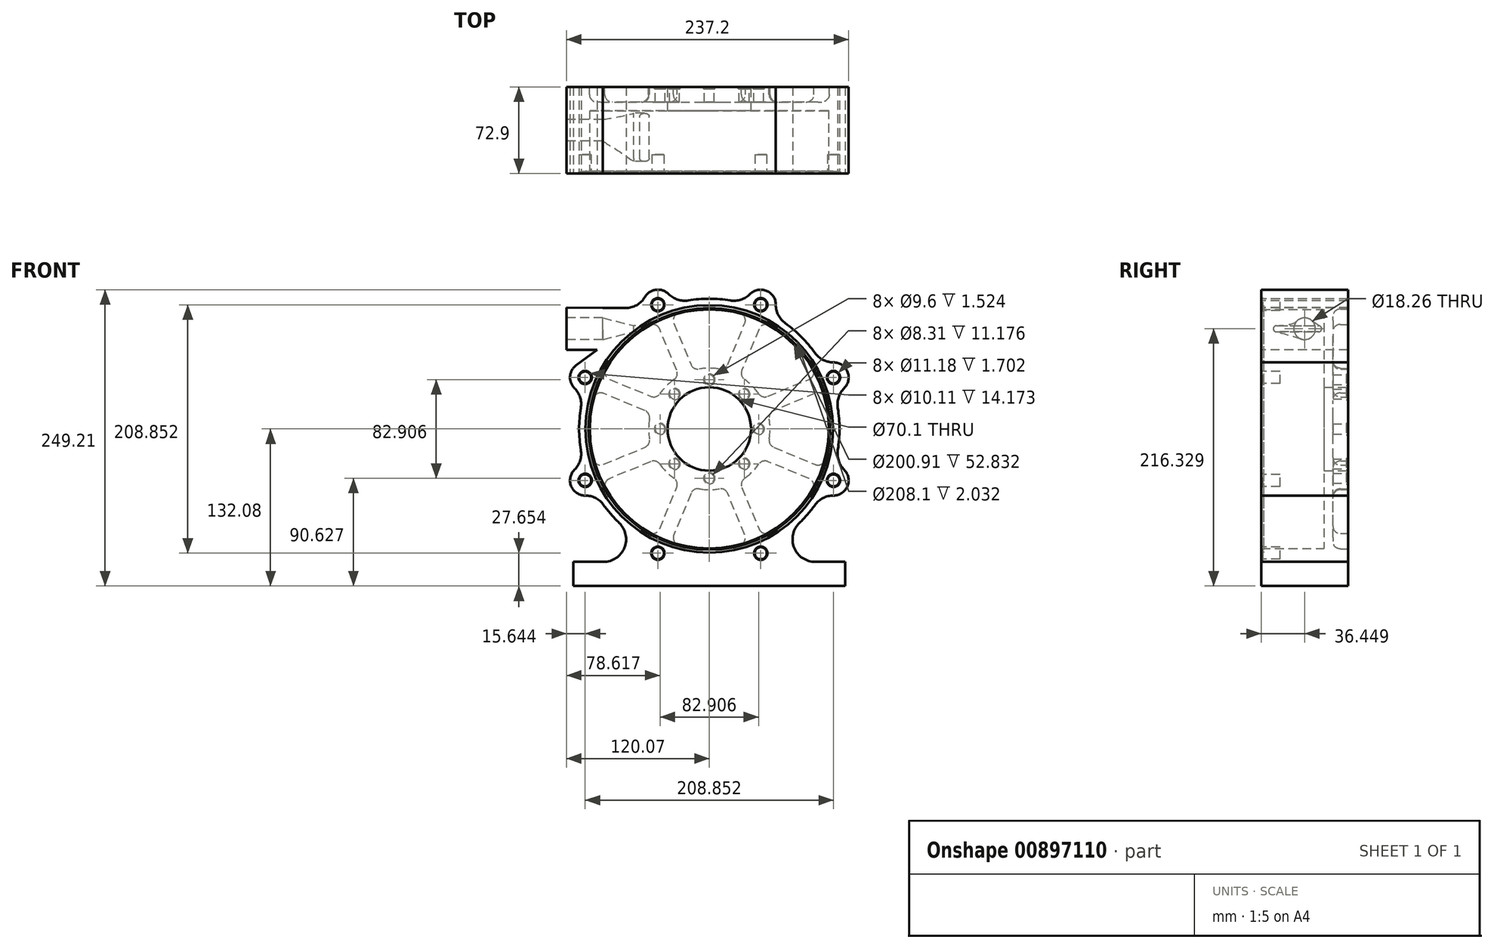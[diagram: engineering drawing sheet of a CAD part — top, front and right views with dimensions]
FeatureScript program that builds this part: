
annotation { "Feature Type Name" : "Feature", "Feature Type Description" : "" }
export const myFeature = defineFeature(function(context is Context, id is Id, definition is map)
    precondition{}
    {
        {
            var Q0;
            Q0=qCreatedBy(makeId("Front.planeOp"),FACE);
            var sketch = newSketch(context, id + "F0", { "sketchPlane" : qUnion([Q0])});
            skCircle(sketch, "E0", {"center": v(0, 0) * mm, "radius": 50.17 * mm, "construction": true});
            skArc(sketch, "E1", {"start": v(54.02, -8.84) * mm, "mid": v(54.74, 0) * mm, "end": v(54.02, 8.84) * mm});
            skCircle(sketch, "E2.cCircle", {"center": v(0, 0) * mm, "radius": 56.52 * mm, "construction": true});
            skLineSegment(sketch, "E2.0", {"start": v(52.21, -21.63) * mm, "end": v(21.63, -52.21) * mm, "construction": true});
            skLineSegment(sketch, "E2.1", {"start": v(21.63, -52.21) * mm, "end": v(-21.63, -52.21) * mm, "construction": true});
            skLineSegment(sketch, "E2.2", {"start": v(-21.63, -52.21) * mm, "end": v(-52.21, -21.63) * mm, "construction": true});
            skLineSegment(sketch, "E2.3", {"start": v(-52.21, -21.63) * mm, "end": v(-52.21, 21.63) * mm, "construction": true});
            skLineSegment(sketch, "E2.4", {"start": v(-52.21, 21.63) * mm, "end": v(-21.63, 52.21) * mm, "construction": true});
            skLineSegment(sketch, "E2.5", {"start": v(-21.63, 52.21) * mm, "end": v(21.63, 52.21) * mm, "construction": true});
            skLineSegment(sketch, "E2.6", {"start": v(21.63, 52.21) * mm, "end": v(52.21, 21.63) * mm, "construction": true});
            skLineSegment(sketch, "E2.7", {"start": v(52.21, 21.63) * mm, "end": v(52.21, -21.63) * mm, "construction": true});
            skArc(sketch, "E3", {"start": v(27.98, 52.2) * mm, "mid": v(24.06, 58.08) * mm, "end": v(17.13, 56.7) * mm});
            skArc(sketch, "E4", {"start": v(56.7, 17.13) * mm, "mid": v(58.08, 24.06) * mm, "end": v(52.2, 27.98) * mm});
            skArc(sketch, "E5", {"start": v(52.2, -27.98) * mm, "mid": v(58.08, -24.06) * mm, "end": v(56.7, -17.13) * mm});
            skArc(sketch, "E6", {"start": v(-56.7, -17.13) * mm, "mid": v(-58.08, -24.06) * mm, "end": v(-52.2, -27.98) * mm});
            skArc(sketch, "E7", {"start": v(-56, 26.73) * mm, "mid": v(-58.55, 22.09) * mm, "end": v(-56.7, 17.13) * mm});
            skArc(sketch, "E8.trimOffspring", {"start": v(44.45, 31.94) * mm, "mid": v(38.7, 38.7) * mm, "end": v(31.94, 44.45) * mm});
            skArc(sketch, "E9.trimOffspring", {"start": v(8.84, 54.02) * mm, "mid": v(0, 54.74) * mm, "end": v(-8.84, 54.02) * mm});
            skArc(sketch, "E10.trimOffspring", {"start": v(-54.02, 8.84) * mm, "mid": v(-54.74, 0) * mm, "end": v(-54.02, -8.84) * mm});
            skArc(sketch, "E11.trimOffspring", {"start": v(-44.45, -31.94) * mm, "mid": v(-41.35, -35.86) * mm, "end": v(-37.9, -39.48) * mm});
            skArc(sketch, "E12.trimOffspring", {"start": v(37.9, -39.48) * mm, "mid": v(41.35, -35.86) * mm, "end": v(44.45, -31.94) * mm});
            skLineSegment(sketch, "E13", {"start": v(-57.15, -55.88) * mm, "end": v(-57.15, -66.04) * mm});
            skLineSegment(sketch, "E14", {"start": v(-57.15, -66.04) * mm, "end": v(57.15, -66.04) * mm});
            skLineSegment(sketch, "E15", {"start": v(57.15, -66.04) * mm, "end": v(57.15, -55.88) * mm});
            skLineSegment(sketch, "E16", {"start": v(57.15, -55.88) * mm, "end": v(44.5, -55.88) * mm});
            skLineSegment(sketch, "E17", {"start": v(-57.15, -55.88) * mm, "end": v(-44.5, -55.88) * mm});
            skPoint(sketch, "E18", {"position": v(0, -66.04) * mm});
            skArc(sketch, "E19", {"start": v(-44.5, -55.88) * mm, "mid": v(-35.67, -49.91) * mm, "end": v(-37.9, -39.48) * mm});
            skArc(sketch, "E20", {"start": v(37.9, -39.48) * mm, "mid": v(35.67, -49.91) * mm, "end": v(44.5, -55.88) * mm});
            skPoint(sketch, "E21.visualSharp", {"position": v(-47.97, -26.36) * mm});
            skArc(sketch, "E21.filletArc", {"start": v(-44.45, -31.94) * mm, "mid": v(-47.85, -29.02) * mm, "end": v(-52.2, -27.98) * mm});
            skPoint(sketch, "E22.visualSharp", {"position": v(-52.56, -15.29) * mm});
            skArc(sketch, "E22.filletArc", {"start": v(-56.7, -17.13) * mm, "mid": v(-54.35, -13.3) * mm, "end": v(-54.02, -8.84) * mm});
            skPoint(sketch, "E23.visualSharp", {"position": v(-52.56, 15.29) * mm});
            skArc(sketch, "E23.filletArc", {"start": v(-54.02, 8.84) * mm, "mid": v(-54.35, 13.3) * mm, "end": v(-56.7, 17.13) * mm});
            skPoint(sketch, "E24.visualSharp", {"position": v(47.97, -26.36) * mm});
            skArc(sketch, "E24.filletArc", {"start": v(52.2, -27.98) * mm, "mid": v(47.85, -29.02) * mm, "end": v(44.45, -31.94) * mm});
            skPoint(sketch, "E25.visualSharp", {"position": v(52.56, -15.29) * mm});
            skArc(sketch, "E25.filletArc", {"start": v(54.02, -8.84) * mm, "mid": v(54.35, -13.3) * mm, "end": v(56.7, -17.13) * mm});
            skPoint(sketch, "E26.visualSharp", {"position": v(52.56, 15.29) * mm});
            skArc(sketch, "E26.filletArc", {"start": v(56.7, 17.13) * mm, "mid": v(54.35, 13.3) * mm, "end": v(54.02, 8.84) * mm});
            skPoint(sketch, "E27.visualSharp", {"position": v(47.97, 26.36) * mm});
            skArc(sketch, "E27.filletArc", {"start": v(44.45, 31.94) * mm, "mid": v(47.85, 29.02) * mm, "end": v(52.2, 27.98) * mm});
            skPoint(sketch, "E28.visualSharp", {"position": v(26.36, 47.97) * mm});
            skArc(sketch, "E28.filletArc", {"start": v(27.98, 52.2) * mm, "mid": v(29.02, 47.85) * mm, "end": v(31.94, 44.45) * mm});
            skPoint(sketch, "E29.visualSharp", {"position": v(15.29, 52.56) * mm});
            skArc(sketch, "E29.filletArc", {"start": v(8.84, 54.02) * mm, "mid": v(13.3, 54.35) * mm, "end": v(17.13, 56.7) * mm});
            skPoint(sketch, "E30.visualSharp", {"position": v(-15.29, 52.56) * mm});
            skLineSegment(sketch, "E31", {"start": v(-35.27, 50.8) * mm, "end": v(-44.8, 50.8) * mm});
            skArc(sketch, "E32", {"start": v(-17.13, 56.7) * mm, "mid": v(-22.41, 58.51) * mm, "end": v(-27.09, 55.46) * mm});
            skArc(sketch, "E33.filletArc", {"start": v(-17.13, 56.7) * mm, "mid": v(-13.3, 54.35) * mm, "end": v(-8.84, 54.02) * mm});
            skPoint(sketch, "E34.visualSharp", {"position": v(-27.82, 50.8) * mm});
            skArc(sketch, "E34.filletArc", {"start": v(-35.27, 50.8) * mm, "mid": v(-30.56, 52.05) * mm, "end": v(-27.09, 55.46) * mm});
            skLineSegment(sketch, "E35", {"start": v(-47.22, 33.23) * mm, "end": v(-56, 26.73) * mm});
            skLineSegment(sketch, "E36", {"start": v(-44.8, 50.8) * mm, "end": v(-60.04, 51.01) * mm});
            skLineSegment(sketch, "E37", {"start": v(-60.04, 51.01) * mm, "end": v(-60.04, 33.23) * mm});
            skLineSegment(sketch, "E38", {"start": v(-60.04, 33.23) * mm, "end": v(-47.22, 33.23) * mm});
            skSolve(sketch);
        }
        {
            var Q0;
            Q0=qSketchRegion(id+"F0",true);
            extrude(context, id + "F1", {"entities" : qUnion([Q0]), "oppositeDirection" : true, "depth" : 36.45 * mm});
        }
        {
            var Q0;
            Q0=qCreatedBy(makeId("Right.planeOp"),FACE);
            var sketch = newSketch(context, id + "F2", { "sketchPlane" : qUnion([Q0])});
            skLineSegment(sketch, "E39", {"start": v(0, 0) * mm, "end": v(0, 50.23) * mm});
            skLineSegment(sketch, "E40", {"start": v(26.42, 50.23) * mm, "end": v(0, 50.23) * mm});
            skLineSegment(sketch, "E41", {"start": v(26.42, 50.23) * mm, "end": v(26.42, 17.53) * mm});
            skLineSegment(sketch, "E42", {"start": v(36.45, 17.53) * mm, "end": v(26.42, 17.53) * mm});
            skLineSegment(sketch, "E43", {"start": v(36.45, 17.53) * mm, "end": v(36.45, 0) * mm});
            skLineSegment(sketch, "E44", {"start": v(0, 0) * mm, "end": v(36.45, 0) * mm});
            skLineSegment(sketch, "E45.bottom", {"start": v(1.02, 50.8) * mm, "end": v(0, 50.8) * mm});
            skLineSegment(sketch, "E45.top", {"start": v(1.02, 52.03) * mm, "end": v(0, 52.03) * mm});
            skLineSegment(sketch, "E45.left", {"start": v(0, 50.8) * mm, "end": v(0, 52.03) * mm});
            skLineSegment(sketch, "E45.right", {"start": v(1.02, 50.8) * mm, "end": v(1.02, 52.03) * mm});
            skSolve(sketch);
        }
        {
            var Q0;
            Q0=qSketchRegion(id+"F2",true);
            var Q1;
            Q1=sQuery(id+"F2.wireOp",EDGE,"E44");
            revolve(context, id + "F3", {"operationType" : NewBodyOperationType.REMOVE, "entities" : qUnion([Q0]), "axis" : qUnion([Q1]), "revolveType" : RevolveType.FULL, "oppositeDirection" : true});
        }
        {
            var Q0;
            Q0=makeQuery(id+"F1.opExtrude","CAP_FACE",FACE,{"disambiguationData":[OSD([sQuery(id+"F0.wireOp",EDGE,"E1"),sQuery(id+"F0.wireOp",EDGE,"E3"),sQuery(id+"F0.wireOp",EDGE,"E4"),sQuery(id+"F0.wireOp",EDGE,"E5"),sQuery(id+"F0.wireOp",EDGE,"E6"),sQuery(id+"F0.wireOp",EDGE,"E7"),sQuery(id+"F0.wireOp",EDGE,"E8.trimOffspring"),sQuery(id+"F0.wireOp",EDGE,"E9.trimOffspring"),sQuery(id+"F0.wireOp",EDGE,"E10.trimOffspring"),sQuery(id+"F0.wireOp",EDGE,"E11.trimOffspring"),sQuery(id+"F0.wireOp",EDGE,"E12.trimOffspring"),sQuery(id+"F0.wireOp",EDGE,"E13"),sQuery(id+"F0.wireOp",EDGE,"E14"),sQuery(id+"F0.wireOp",EDGE,"E15"),sQuery(id+"F0.wireOp",EDGE,"E16"),sQuery(id+"F0.wireOp",EDGE,"E17"),sQuery(id+"F0.wireOp",EDGE,"E19"),sQuery(id+"F0.wireOp",EDGE,"E20"),sQuery(id+"F0.wireOp",EDGE,"E21.filletArc"),sQuery(id+"F0.wireOp",EDGE,"E22.filletArc"),sQuery(id+"F0.wireOp",EDGE,"E23.filletArc"),sQuery(id+"F0.wireOp",EDGE,"E24.filletArc"),sQuery(id+"F0.wireOp",EDGE,"E25.filletArc"),sQuery(id+"F0.wireOp",EDGE,"E26.filletArc"),sQuery(id+"F0.wireOp",EDGE,"E27.filletArc"),sQuery(id+"F0.wireOp",EDGE,"E28.filletArc"),sQuery(id+"F0.wireOp",EDGE,"E29.filletArc"),sQuery(id+"F0.wireOp",EDGE,"E31"),sQuery(id+"F0.wireOp",EDGE,"kHr8fFUD-4EFk-nJZE-7JVT-0WPmz8yTTr2E"),sQuery(id+"F0.wireOp",EDGE,"E32"),sQuery(id+"F0.wireOp",EDGE,"E33.filletArc"),sQuery(id+"F0.wireOp",EDGE,"E34.filletArc"),sQuery(id+"F0.wireOp",EDGE,"fBgQRkSS-CIUt-JJdx-RIVp-XrYWp9c1mPRc"),sQuery(id+"F0.wireOp",EDGE,"E35")])],"isStart":false});
            var sketch = newSketch(context, id + "F4", { "sketchPlane" : qUnion([Q0])});
            skPoint(sketch, "E46.center", {"position": v(0, 0) * mm});
            skArc(sketch, "E47", {"start": v(4.25, 25.17) * mm, "mid": v(0, 25.53) * mm, "end": v(-4.25, 25.17) * mm});
            skLineSegment(sketch, "E48", {"start": v(0, 0) * mm, "end": v(24.06, 58.08) * mm, "construction": true});
            skLineSegment(sketch, "E49", {"start": v(0, 0) * mm, "end": v(0, 17.53) * mm, "construction": true});
            skArc(sketch, "E50", {"start": v(12.8, 48.77) * mm, "mid": v(0, 50.42) * mm, "end": v(-12.8, 48.77) * mm});
            skLineSegment(sketch, "E51", {"start": v(14.92, 44.48) * mm, "end": v(7.71, 27.09) * mm});
            skLineSegment(sketch, "E52", {"start": v(-7.71, 27.09) * mm, "end": v(-14.92, 44.48) * mm});
            skPoint(sketch, "E53.visualSharp", {"position": v(-16.26, 47.72) * mm});
            skArc(sketch, "E53.filletArc", {"start": v(-12.8, 48.77) * mm, "mid": v(-14.83, 47.1) * mm, "end": v(-14.92, 44.48) * mm});
            skPoint(sketch, "E54.visualSharp", {"position": v(16.26, 47.72) * mm});
            skArc(sketch, "E54.filletArc", {"start": v(14.92, 44.48) * mm, "mid": v(14.83, 47.1) * mm, "end": v(12.8, 48.77) * mm});
            skPoint(sketch, "E55.visualSharp", {"position": v(6.7, 24.63) * mm});
            skArc(sketch, "E55.filletArc", {"start": v(4.25, 25.17) * mm, "mid": v(6.32, 25.52) * mm, "end": v(7.71, 27.09) * mm});
            skPoint(sketch, "E56.visualSharp", {"position": v(-6.7, 24.63) * mm});
            skArc(sketch, "E56.filletArc", {"start": v(-7.71, 27.09) * mm, "mid": v(-6.32, 25.52) * mm, "end": v(-4.25, 25.17) * mm});
            skArc(sketch, "E57.1.0", {"start": v(-43.53, 25.44) * mm, "mid": v(-43.8, 22.82) * mm, "end": v(-42, 20.9) * mm});
            skLineSegment(sketch, "E57.1.1", {"start": v(-24.6, 13.7) * mm, "end": v(-42, 20.9) * mm});
            skArc(sketch, "E57.1.2", {"start": v(-14.8, 20.8) * mm, "mid": v(-18.05, 18.05) * mm, "end": v(-20.8, 14.8) * mm});
            skArc(sketch, "E57.1.3", {"start": v(-24.6, 13.7) * mm, "mid": v(-22.51, 13.58) * mm, "end": v(-20.8, 14.8) * mm});
            skArc(sketch, "E57.1.4", {"start": v(-14.8, 20.8) * mm, "mid": v(-13.58, 22.51) * mm, "end": v(-13.7, 24.6) * mm});
            skLineSegment(sketch, "E57.1.5", {"start": v(-20.9, 42) * mm, "end": v(-13.7, 24.6) * mm});
            skArc(sketch, "E57.1.6", {"start": v(-20.9, 42) * mm, "mid": v(-22.82, 43.8) * mm, "end": v(-25.44, 43.53) * mm});
            skArc(sketch, "E57.1.7", {"start": v(-25.44, 43.53) * mm, "mid": v(-35.65, 35.65) * mm, "end": v(-43.53, 25.44) * mm});
            skArc(sketch, "E57.2.0", {"start": v(-48.77, -12.8) * mm, "mid": v(-47.1, -14.83) * mm, "end": v(-44.48, -14.92) * mm});
            skLineSegment(sketch, "E57.2.1", {"start": v(-27.09, -7.71) * mm, "end": v(-44.48, -14.92) * mm});
            skArc(sketch, "E57.2.2", {"start": v(-25.17, 4.25) * mm, "mid": v(-25.53, 0) * mm, "end": v(-25.17, -4.25) * mm});
            skArc(sketch, "E57.2.3", {"start": v(-27.09, -7.71) * mm, "mid": v(-25.52, -6.32) * mm, "end": v(-25.17, -4.25) * mm});
            skArc(sketch, "E57.2.4", {"start": v(-25.17, 4.25) * mm, "mid": v(-25.52, 6.32) * mm, "end": v(-27.09, 7.71) * mm});
            skLineSegment(sketch, "E57.2.5", {"start": v(-44.48, 14.92) * mm, "end": v(-27.09, 7.71) * mm});
            skArc(sketch, "E57.2.6", {"start": v(-44.48, 14.92) * mm, "mid": v(-47.1, 14.83) * mm, "end": v(-48.77, 12.8) * mm});
            skArc(sketch, "E57.2.7", {"start": v(-48.77, 12.8) * mm, "mid": v(-50.42, 0) * mm, "end": v(-48.77, -12.8) * mm});
            skArc(sketch, "E57.3.0", {"start": v(-25.44, -43.53) * mm, "mid": v(-22.82, -43.8) * mm, "end": v(-20.9, -42) * mm});
            skLineSegment(sketch, "E57.3.1", {"start": v(-13.7, -24.6) * mm, "end": v(-20.9, -42) * mm});
            skArc(sketch, "E57.3.2", {"start": v(-20.8, -14.8) * mm, "mid": v(-18.05, -18.05) * mm, "end": v(-14.8, -20.8) * mm});
            skArc(sketch, "E57.3.3", {"start": v(-13.7, -24.6) * mm, "mid": v(-13.58, -22.51) * mm, "end": v(-14.8, -20.8) * mm});
            skArc(sketch, "E57.3.4", {"start": v(-20.8, -14.8) * mm, "mid": v(-22.51, -13.58) * mm, "end": v(-24.6, -13.7) * mm});
            skLineSegment(sketch, "E57.3.5", {"start": v(-42, -20.9) * mm, "end": v(-24.6, -13.7) * mm});
            skArc(sketch, "E57.3.6", {"start": v(-42, -20.9) * mm, "mid": v(-43.8, -22.82) * mm, "end": v(-43.53, -25.44) * mm});
            skArc(sketch, "E57.3.7", {"start": v(-43.53, -25.44) * mm, "mid": v(-35.65, -35.65) * mm, "end": v(-25.44, -43.53) * mm});
            skArc(sketch, "E57.4.0", {"start": v(12.8, -48.77) * mm, "mid": v(14.83, -47.1) * mm, "end": v(14.92, -44.48) * mm});
            skLineSegment(sketch, "E57.4.1", {"start": v(7.71, -27.09) * mm, "end": v(14.92, -44.48) * mm});
            skArc(sketch, "E57.4.2", {"start": v(-4.25, -25.17) * mm, "mid": v(0, -25.53) * mm, "end": v(4.25, -25.17) * mm});
            skArc(sketch, "E57.4.3", {"start": v(7.71, -27.09) * mm, "mid": v(6.32, -25.52) * mm, "end": v(4.25, -25.17) * mm});
            skArc(sketch, "E57.4.4", {"start": v(-4.25, -25.17) * mm, "mid": v(-6.32, -25.52) * mm, "end": v(-7.71, -27.09) * mm});
            skLineSegment(sketch, "E57.4.5", {"start": v(-14.92, -44.48) * mm, "end": v(-7.71, -27.09) * mm});
            skArc(sketch, "E57.4.6", {"start": v(-14.92, -44.48) * mm, "mid": v(-14.83, -47.1) * mm, "end": v(-12.8, -48.77) * mm});
            skArc(sketch, "E57.4.7", {"start": v(-12.8, -48.77) * mm, "mid": v(0, -50.42) * mm, "end": v(12.8, -48.77) * mm});
            skArc(sketch, "E57.5.0", {"start": v(43.53, -25.44) * mm, "mid": v(43.8, -22.82) * mm, "end": v(42, -20.9) * mm});
            skLineSegment(sketch, "E57.5.1", {"start": v(24.6, -13.7) * mm, "end": v(42, -20.9) * mm});
            skArc(sketch, "E57.5.2", {"start": v(14.8, -20.8) * mm, "mid": v(18.05, -18.05) * mm, "end": v(20.8, -14.8) * mm});
            skArc(sketch, "E57.5.3", {"start": v(24.6, -13.7) * mm, "mid": v(22.51, -13.58) * mm, "end": v(20.8, -14.8) * mm});
            skArc(sketch, "E57.5.4", {"start": v(14.8, -20.8) * mm, "mid": v(13.58, -22.51) * mm, "end": v(13.7, -24.6) * mm});
            skLineSegment(sketch, "E57.5.5", {"start": v(20.9, -42) * mm, "end": v(13.7, -24.6) * mm});
            skArc(sketch, "E57.5.6", {"start": v(20.9, -42) * mm, "mid": v(22.82, -43.8) * mm, "end": v(25.44, -43.53) * mm});
            skArc(sketch, "E57.5.7", {"start": v(25.44, -43.53) * mm, "mid": v(35.65, -35.65) * mm, "end": v(43.53, -25.44) * mm});
            skArc(sketch, "E57.6.0", {"start": v(48.77, 12.8) * mm, "mid": v(47.1, 14.83) * mm, "end": v(44.48, 14.92) * mm});
            skLineSegment(sketch, "E57.6.1", {"start": v(27.09, 7.71) * mm, "end": v(44.48, 14.92) * mm});
            skArc(sketch, "E57.6.2", {"start": v(25.17, -4.25) * mm, "mid": v(25.53, 0) * mm, "end": v(25.17, 4.25) * mm});
            skArc(sketch, "E57.6.3", {"start": v(27.09, 7.71) * mm, "mid": v(25.52, 6.32) * mm, "end": v(25.17, 4.25) * mm});
            skArc(sketch, "E57.6.4", {"start": v(25.17, -4.25) * mm, "mid": v(25.52, -6.32) * mm, "end": v(27.09, -7.71) * mm});
            skLineSegment(sketch, "E57.6.5", {"start": v(44.48, -14.92) * mm, "end": v(27.09, -7.71) * mm});
            skArc(sketch, "E57.6.6", {"start": v(44.48, -14.92) * mm, "mid": v(47.1, -14.83) * mm, "end": v(48.77, -12.8) * mm});
            skArc(sketch, "E57.6.7", {"start": v(48.77, -12.8) * mm, "mid": v(50.42, 0) * mm, "end": v(48.77, 12.8) * mm});
            skArc(sketch, "E57.7.0", {"start": v(25.44, 43.53) * mm, "mid": v(22.82, 43.8) * mm, "end": v(20.9, 42) * mm});
            skLineSegment(sketch, "E57.7.1", {"start": v(13.7, 24.6) * mm, "end": v(20.9, 42) * mm});
            skArc(sketch, "E57.7.2", {"start": v(20.8, 14.8) * mm, "mid": v(18.05, 18.05) * mm, "end": v(14.8, 20.8) * mm});
            skArc(sketch, "E57.7.3", {"start": v(13.7, 24.6) * mm, "mid": v(13.58, 22.51) * mm, "end": v(14.8, 20.8) * mm});
            skArc(sketch, "E57.7.4", {"start": v(20.8, 14.8) * mm, "mid": v(22.51, 13.58) * mm, "end": v(24.6, 13.7) * mm});
            skLineSegment(sketch, "E57.7.5", {"start": v(42, 20.9) * mm, "end": v(24.6, 13.7) * mm});
            skArc(sketch, "E57.7.6", {"start": v(42, 20.9) * mm, "mid": v(43.8, 22.82) * mm, "end": v(43.53, 25.44) * mm});
            skArc(sketch, "E57.7.7", {"start": v(43.53, 25.44) * mm, "mid": v(35.65, 35.65) * mm, "end": v(25.44, 43.53) * mm});
            skSolve(sketch);
        }
        {
            var Q0;
            Q0=qSketchRegion(id+"F4",true);
            extrude(context, id + "F5", {"entities" : qUnion([Q0]), "operationType" : NewBodyOperationType.REMOVE, "oppositeDirection" : true, "depth" : 6.35 * mm});
        }
        {
            var Q0;
            Q0=makeQuery(id+"F5.boolean.opBoolean","COPY",FACE,{"derivedFrom":makeQuery(id+"F5.opExtrude","CAP_FACE",FACE,{"disambiguationData":[OSD([sQuery(id+"F4.wireOp",EDGE,"E47"),sQuery(id+"F4.wireOp",EDGE,"E50"),sQuery(id+"F4.wireOp",EDGE,"E51"),sQuery(id+"F4.wireOp",EDGE,"E52"),sQuery(id+"F4.wireOp",EDGE,"E53.filletArc"),sQuery(id+"F4.wireOp",EDGE,"E54.filletArc"),sQuery(id+"F4.wireOp",EDGE,"E55.filletArc"),sQuery(id+"F4.wireOp",EDGE,"E56.filletArc")])],"isStart":false})});
            var Q1;
            Q1=makeQuery(id+"F5.boolean.opBoolean","COPY",FACE,{"derivedFrom":makeQuery(id+"F5.opExtrude","CAP_FACE",FACE,{"disambiguationData":[OSD([sQuery(id+"F4.wireOp",EDGE,"E57.7.0"),sQuery(id+"F4.wireOp",EDGE,"E57.7.1"),sQuery(id+"F4.wireOp",EDGE,"E57.7.2"),sQuery(id+"F4.wireOp",EDGE,"E57.7.3"),sQuery(id+"F4.wireOp",EDGE,"E57.7.4"),sQuery(id+"F4.wireOp",EDGE,"E57.7.5"),sQuery(id+"F4.wireOp",EDGE,"E57.7.6"),sQuery(id+"F4.wireOp",EDGE,"E57.7.7")])],"isStart":false})});
            var Q2;
            Q2=makeQuery(id+"F5.boolean.opBoolean","COPY",FACE,{"derivedFrom":makeQuery(id+"F5.opExtrude","CAP_FACE",FACE,{"disambiguationData":[OSD([sQuery(id+"F4.wireOp",EDGE,"E57.6.0"),sQuery(id+"F4.wireOp",EDGE,"E57.6.1"),sQuery(id+"F4.wireOp",EDGE,"E57.6.2"),sQuery(id+"F4.wireOp",EDGE,"E57.6.3"),sQuery(id+"F4.wireOp",EDGE,"E57.6.4"),sQuery(id+"F4.wireOp",EDGE,"E57.6.5"),sQuery(id+"F4.wireOp",EDGE,"E57.6.6"),sQuery(id+"F4.wireOp",EDGE,"E57.6.7")])],"isStart":false})});
            var Q3;
            Q3=makeQuery(id+"F5.boolean.opBoolean","COPY",FACE,{"derivedFrom":makeQuery(id+"F5.opExtrude","CAP_FACE",FACE,{"disambiguationData":[OSD([sQuery(id+"F4.wireOp",EDGE,"E57.5.0"),sQuery(id+"F4.wireOp",EDGE,"E57.5.1"),sQuery(id+"F4.wireOp",EDGE,"E57.5.2"),sQuery(id+"F4.wireOp",EDGE,"E57.5.3"),sQuery(id+"F4.wireOp",EDGE,"E57.5.4"),sQuery(id+"F4.wireOp",EDGE,"E57.5.5"),sQuery(id+"F4.wireOp",EDGE,"E57.5.6"),sQuery(id+"F4.wireOp",EDGE,"E57.5.7")])],"isStart":false})});
            var Q4;
            Q4=makeQuery(id+"F5.boolean.opBoolean","COPY",FACE,{"derivedFrom":makeQuery(id+"F5.opExtrude","CAP_FACE",FACE,{"disambiguationData":[OSD([sQuery(id+"F4.wireOp",EDGE,"E57.4.0"),sQuery(id+"F4.wireOp",EDGE,"E57.4.1"),sQuery(id+"F4.wireOp",EDGE,"E57.4.2"),sQuery(id+"F4.wireOp",EDGE,"E57.4.3"),sQuery(id+"F4.wireOp",EDGE,"E57.4.4"),sQuery(id+"F4.wireOp",EDGE,"E57.4.5"),sQuery(id+"F4.wireOp",EDGE,"E57.4.6"),sQuery(id+"F4.wireOp",EDGE,"E57.4.7")])],"isStart":false})});
            var Q5;
            Q5=makeQuery(id+"F5.boolean.opBoolean","COPY",FACE,{"derivedFrom":makeQuery(id+"F5.opExtrude","CAP_FACE",FACE,{"disambiguationData":[OSD([sQuery(id+"F4.wireOp",EDGE,"E57.3.0"),sQuery(id+"F4.wireOp",EDGE,"E57.3.1"),sQuery(id+"F4.wireOp",EDGE,"E57.3.2"),sQuery(id+"F4.wireOp",EDGE,"E57.3.3"),sQuery(id+"F4.wireOp",EDGE,"E57.3.4"),sQuery(id+"F4.wireOp",EDGE,"E57.3.5"),sQuery(id+"F4.wireOp",EDGE,"E57.3.6"),sQuery(id+"F4.wireOp",EDGE,"E57.3.7")])],"isStart":false})});
            var Q6;
            Q6=makeQuery(id+"F5.boolean.opBoolean","COPY",FACE,{"derivedFrom":makeQuery(id+"F5.opExtrude","CAP_FACE",FACE,{"disambiguationData":[OSD([sQuery(id+"F4.wireOp",EDGE,"E57.2.0"),sQuery(id+"F4.wireOp",EDGE,"E57.2.1"),sQuery(id+"F4.wireOp",EDGE,"E57.2.2"),sQuery(id+"F4.wireOp",EDGE,"E57.2.3"),sQuery(id+"F4.wireOp",EDGE,"E57.2.4"),sQuery(id+"F4.wireOp",EDGE,"E57.2.5"),sQuery(id+"F4.wireOp",EDGE,"E57.2.6"),sQuery(id+"F4.wireOp",EDGE,"E57.2.7")])],"isStart":false})});
            var Q7;
            Q7=makeQuery(id+"F5.boolean.opBoolean","COPY",FACE,{"derivedFrom":makeQuery(id+"F5.opExtrude","CAP_FACE",FACE,{"disambiguationData":[OSD([sQuery(id+"F4.wireOp",EDGE,"E57.1.0"),sQuery(id+"F4.wireOp",EDGE,"E57.1.1"),sQuery(id+"F4.wireOp",EDGE,"E57.1.2"),sQuery(id+"F4.wireOp",EDGE,"E57.1.3"),sQuery(id+"F4.wireOp",EDGE,"E57.1.4"),sQuery(id+"F4.wireOp",EDGE,"E57.1.5"),sQuery(id+"F4.wireOp",EDGE,"E57.1.6"),sQuery(id+"F4.wireOp",EDGE,"E57.1.7")])],"isStart":false})});
            fillet(context, id + "F6", {"entities" : qUnion([Q0, Q1, Q2, Q3, Q4, Q5, Q6, Q7]), "radius" : 3.17 * mm, "tangentPropagation" : true, "allowEdgeOverflow" : false});
        }
        {
            var Q0;
            Q0=makeQuery(id+"F1.opExtrude","SWEPT_FACE",FACE,{"disambiguationData":[OSD([sQuery(id+"F0.wireOp",EDGE,"E37")])]});
            var sketch = newSketch(context, id + "F7", { "sketchPlane" : qUnion([Q0])});
            skCircle(sketch, "E58", {"center": v(-18.22, 42.12) * mm, "radius": 4.56 * mm});
            skPoint(sketch, "E59", {"position": v(-18.22, 51.01) * mm});
            skPoint(sketch, "E60", {"position": v(0, 42.12) * mm});
            skSolve(sketch);
        }
        {
            var Q0;
            Q0=qSketchRegion(id+"F7",true);
            extrude(context, id + "F8", {"entities" : qUnion([Q0]), "operationType" : NewBodyOperationType.REMOVE, "oppositeDirection" : true, "depth" : 15.24 * mm});
        }
        {
            var Q0;
            Q0=qCreatedBy(makeId("Right.planeOp"),FACE);
            cPlane(context, id + "F9", {"entities" : qUnion([Q0]), "cplaneType" : CPlaneType.OFFSET, "offset" : 31.75 * mm, "oppositeDirection" : true, "width" : 152.4 * mm, "height" : 152.4 * mm});
        }
        {
            var Q0;
            Q0=qCreatedBy(id+"F9.planeOp",FACE);
            var sketch = newSketch(context, id + "F10", { "sketchPlane" : qUnion([Q0])});
            skLineSegment(sketch, "E61", {"start": v(6.35, 43.4) * mm, "end": v(24.13, 43.4) * mm});
            skLineSegment(sketch, "E62", {"start": v(24.13, 40.85) * mm, "end": v(6.35, 40.85) * mm});
            skArc(sketch, "E63", {"start": v(24.13, 40.85) * mm, "mid": v(25.4, 42.12) * mm, "end": v(24.13, 43.4) * mm});
            skArc(sketch, "E64", {"start": v(6.35, 43.4) * mm, "mid": v(5.08, 42.12) * mm, "end": v(6.35, 40.85) * mm});
            skPoint(sketch, "E65", {"position": v(18.22, 42.12) * mm});
            skSolve(sketch);
        }
        {
            var Q0;
            Q0=makeQuery(id+"F8.boolean.opBoolean","COPY",FACE,{"derivedFrom":makeQuery(id+"F8.opExtrude","CAP_FACE",FACE,{"disambiguationData":[OSD([sQuery(id+"F7.wireOp",EDGE,"E58")])],"isStart":false})});
            var sketch = newSketch(context, id + "F11", { "sketchPlane" : qUnion([Q0])});
            skCircle(sketch, "E66", {"center": v(-18.22, 42.12) * mm, "radius": 4.56 * mm});
            skSolve(sketch);
        }
        {
            var Q1;
            Q1=qSketchRegion(id+"F10",true);
            var Q2;
            Q2=qSketchRegion(id+"F11",true);
            loft(context, id + "F12", {"operationType" : NewBodyOperationType.REMOVE, "sheetProfilesArray" : [{ "sheetProfileEntities" : qUnion([Q1]) }, { "sheetProfileEntities" : qUnion([Q2]) }]});
        }
        {
            var Q0;
            Q0=qSketchRegion(id+"F10",true);
            extrude(context, id + "F13", {"entities" : qUnion([Q0]), "operationType" : NewBodyOperationType.REMOVE, "depth" : 25.4 * mm});
        }
        {
            var Q0;
            Q0=makeQuery(id+"F1.opExtrude","SWEPT_BODY",BODY,{"disambiguationData":[OSD([sQuery(id+"F0.wireOp",EDGE,"E1"),sQuery(id+"F0.wireOp",EDGE,"E3"),sQuery(id+"F0.wireOp",EDGE,"E4"),sQuery(id+"F0.wireOp",EDGE,"E5"),sQuery(id+"F0.wireOp",EDGE,"E6"),sQuery(id+"F0.wireOp",EDGE,"E7"),sQuery(id+"F0.wireOp",EDGE,"E8.trimOffspring"),sQuery(id+"F0.wireOp",EDGE,"E9.trimOffspring"),sQuery(id+"F0.wireOp",EDGE,"E10.trimOffspring"),sQuery(id+"F0.wireOp",EDGE,"E11.trimOffspring"),sQuery(id+"F0.wireOp",EDGE,"E12.trimOffspring"),sQuery(id+"F0.wireOp",EDGE,"E13"),sQuery(id+"F0.wireOp",EDGE,"E14"),sQuery(id+"F0.wireOp",EDGE,"E15"),sQuery(id+"F0.wireOp",EDGE,"E16"),sQuery(id+"F0.wireOp",EDGE,"E17"),sQuery(id+"F0.wireOp",EDGE,"E19"),sQuery(id+"F0.wireOp",EDGE,"E20"),sQuery(id+"F0.wireOp",EDGE,"E21.filletArc"),sQuery(id+"F0.wireOp",EDGE,"E22.filletArc"),sQuery(id+"F0.wireOp",EDGE,"E23.filletArc"),sQuery(id+"F0.wireOp",EDGE,"E24.filletArc"),sQuery(id+"F0.wireOp",EDGE,"E25.filletArc"),sQuery(id+"F0.wireOp",EDGE,"E26.filletArc"),sQuery(id+"F0.wireOp",EDGE,"E27.filletArc"),sQuery(id+"F0.wireOp",EDGE,"E28.filletArc"),sQuery(id+"F0.wireOp",EDGE,"E29.filletArc"),sQuery(id+"F0.wireOp",EDGE,"E31"),sQuery(id+"F0.wireOp",EDGE,"E32"),sQuery(id+"F0.wireOp",EDGE,"E33.filletArc"),sQuery(id+"F0.wireOp",EDGE,"E34.filletArc"),sQuery(id+"F0.wireOp",EDGE,"E35"),sQuery(id+"F0.wireOp",EDGE,"E36"),sQuery(id+"F0.wireOp",EDGE,"E37"),sQuery(id+"F0.wireOp",EDGE,"E38")])]});
            var Q1;
            Q1=qCreatedBy(makeId("Origin.pointOp"),VERTEX);
            transform(context, id + "F14", {"entities" : qUnion([Q0]), "transformType" : TransformType.SCALE_UNIFORMLY, "scale" : 2, "scalePoint" : qUnion([Q1]), "makeCopy" : false});
        }
        {
            var Q0;
            Q0=makeQuery(id+"F1.opExtrude","CAP_FACE",FACE,{"disambiguationData":[OSD([sQuery(id+"F0.wireOp",EDGE,"E1"),sQuery(id+"F0.wireOp",EDGE,"E3"),sQuery(id+"F0.wireOp",EDGE,"E4"),sQuery(id+"F0.wireOp",EDGE,"E5"),sQuery(id+"F0.wireOp",EDGE,"E6"),sQuery(id+"F0.wireOp",EDGE,"E7"),sQuery(id+"F0.wireOp",EDGE,"E8.trimOffspring"),sQuery(id+"F0.wireOp",EDGE,"E9.trimOffspring"),sQuery(id+"F0.wireOp",EDGE,"E10.trimOffspring"),sQuery(id+"F0.wireOp",EDGE,"E11.trimOffspring"),sQuery(id+"F0.wireOp",EDGE,"E12.trimOffspring"),sQuery(id+"F0.wireOp",EDGE,"E13"),sQuery(id+"F0.wireOp",EDGE,"E14"),sQuery(id+"F0.wireOp",EDGE,"E15"),sQuery(id+"F0.wireOp",EDGE,"E16"),sQuery(id+"F0.wireOp",EDGE,"E17"),sQuery(id+"F0.wireOp",EDGE,"E19"),sQuery(id+"F0.wireOp",EDGE,"E20"),sQuery(id+"F0.wireOp",EDGE,"E21.filletArc"),sQuery(id+"F0.wireOp",EDGE,"E22.filletArc"),sQuery(id+"F0.wireOp",EDGE,"E23.filletArc"),sQuery(id+"F0.wireOp",EDGE,"E24.filletArc"),sQuery(id+"F0.wireOp",EDGE,"E25.filletArc"),sQuery(id+"F0.wireOp",EDGE,"E26.filletArc"),sQuery(id+"F0.wireOp",EDGE,"E27.filletArc"),sQuery(id+"F0.wireOp",EDGE,"E28.filletArc"),sQuery(id+"F0.wireOp",EDGE,"E29.filletArc"),sQuery(id+"F0.wireOp",EDGE,"E31"),sQuery(id+"F0.wireOp",EDGE,"kHr8fFUD-4EFk-nJZE-7JVT-0WPmz8yTTr2E"),sQuery(id+"F0.wireOp",EDGE,"E32"),sQuery(id+"F0.wireOp",EDGE,"E33.filletArc"),sQuery(id+"F0.wireOp",EDGE,"E34.filletArc"),sQuery(id+"F0.wireOp",EDGE,"fBgQRkSS-CIUt-JJdx-RIVp-XrYWp9c1mPRc"),sQuery(id+"F0.wireOp",EDGE,"E35")])],"isStart":false});
            var sketch = newSketch(context, id + "F15", { "sketchPlane" : qUnion([Q0])});
            skCircle(sketch, "E67", {"center": v(0, 41.45) * mm, "radius": 4.15 * mm});
            skCircle(sketch, "E68.1.0", {"center": v(-29.31, 29.31) * mm, "radius": 4.15 * mm});
            skCircle(sketch, "E68.2.0", {"center": v(-41.45, 0) * mm, "radius": 4.15 * mm});
            skCircle(sketch, "E68.3.0", {"center": v(-29.31, -29.31) * mm, "radius": 4.15 * mm});
            skCircle(sketch, "E68.4.0", {"center": v(0, -41.45) * mm, "radius": 4.15 * mm});
            skCircle(sketch, "E68.5.0", {"center": v(29.31, -29.31) * mm, "radius": 4.15 * mm});
            skCircle(sketch, "E68.6.0", {"center": v(41.45, 0) * mm, "radius": 4.15 * mm});
            skCircle(sketch, "E68.7.0", {"center": v(29.31, 29.31) * mm, "radius": 4.15 * mm});
            skPoint(sketch, "E68.center", {"position": v(0, 0) * mm});
            skSolve(sketch);
        }
        {
            var Q0;
            Q0=qSketchRegion(id+"F15",true);
            extrude(context, id + "F16", {"entities" : qUnion([Q0]), "operationType" : NewBodyOperationType.REMOVE, "oppositeDirection" : true, "depth" : 12.7 * mm});
        }
        {
            var Q0;
            Q0=makeQuery(id+"F1.opExtrude","CAP_FACE",FACE,{"disambiguationData":[OSD([sQuery(id+"F0.wireOp",EDGE,"E1"),sQuery(id+"F0.wireOp",EDGE,"E3"),sQuery(id+"F0.wireOp",EDGE,"E4"),sQuery(id+"F0.wireOp",EDGE,"E5"),sQuery(id+"F0.wireOp",EDGE,"E6"),sQuery(id+"F0.wireOp",EDGE,"E7"),sQuery(id+"F0.wireOp",EDGE,"E8.trimOffspring"),sQuery(id+"F0.wireOp",EDGE,"E9.trimOffspring"),sQuery(id+"F0.wireOp",EDGE,"E10.trimOffspring"),sQuery(id+"F0.wireOp",EDGE,"E11.trimOffspring"),sQuery(id+"F0.wireOp",EDGE,"E12.trimOffspring"),sQuery(id+"F0.wireOp",EDGE,"E13"),sQuery(id+"F0.wireOp",EDGE,"E14"),sQuery(id+"F0.wireOp",EDGE,"E15"),sQuery(id+"F0.wireOp",EDGE,"E16"),sQuery(id+"F0.wireOp",EDGE,"E17"),sQuery(id+"F0.wireOp",EDGE,"E19"),sQuery(id+"F0.wireOp",EDGE,"E20"),sQuery(id+"F0.wireOp",EDGE,"E21.filletArc"),sQuery(id+"F0.wireOp",EDGE,"E22.filletArc"),sQuery(id+"F0.wireOp",EDGE,"E23.filletArc"),sQuery(id+"F0.wireOp",EDGE,"E24.filletArc"),sQuery(id+"F0.wireOp",EDGE,"E25.filletArc"),sQuery(id+"F0.wireOp",EDGE,"E26.filletArc"),sQuery(id+"F0.wireOp",EDGE,"E27.filletArc"),sQuery(id+"F0.wireOp",EDGE,"E28.filletArc"),sQuery(id+"F0.wireOp",EDGE,"E29.filletArc"),sQuery(id+"F0.wireOp",EDGE,"E31"),sQuery(id+"F0.wireOp",EDGE,"E32"),sQuery(id+"F0.wireOp",EDGE,"E33.filletArc"),sQuery(id+"F0.wireOp",EDGE,"E34.filletArc"),sQuery(id+"F0.wireOp",EDGE,"E35"),sQuery(id+"F0.wireOp",EDGE,"E36"),sQuery(id+"F0.wireOp",EDGE,"E37"),sQuery(id+"F0.wireOp",EDGE,"E38")])],"isStart":false});
            var sketch = newSketch(context, id + "F17", { "sketchPlane" : qUnion([Q0])});
            skCircle(sketch, "E69", {"center": v(0, 41.45) * mm, "radius": 4.8 * mm});
            skCircle(sketch, "E70.1.0", {"center": v(-29.31, 29.31) * mm, "radius": 4.8 * mm});
            skCircle(sketch, "E70.2.0", {"center": v(-41.45, 0) * mm, "radius": 4.8 * mm});
            skCircle(sketch, "E70.3.0", {"center": v(-29.31, -29.31) * mm, "radius": 4.8 * mm});
            skCircle(sketch, "E70.4.0", {"center": v(0, -41.45) * mm, "radius": 4.8 * mm});
            skCircle(sketch, "E70.5.0", {"center": v(29.31, -29.31) * mm, "radius": 4.8 * mm});
            skCircle(sketch, "E70.6.0", {"center": v(41.45, 0) * mm, "radius": 4.8 * mm});
            skCircle(sketch, "E70.7.0", {"center": v(29.31, 29.31) * mm, "radius": 4.8 * mm});
            skPoint(sketch, "E70.center", {"position": v(0, 0) * mm});
            skSolve(sketch);
        }
        {
            var Q0;
            Q0=qSketchRegion(id+"F17",true);
            extrude(context, id + "F18", {"entities" : qUnion([Q0]), "operationType" : NewBodyOperationType.REMOVE, "oppositeDirection" : true, "depth" : 1.52 * mm});
        }
        {
            var Q0;
            Q0=qCreatedBy(makeId("Front.planeOp"),FACE);
            var sketch = newSketch(context, id + "F19", { "sketchPlane" : qUnion([Q0])});
            skCircle(sketch, "E71", {"center": v(43.25, 104.43) * mm, "radius": 5.05 * mm});
            skCircle(sketch, "E72.1.0", {"center": v(-43.25, 104.43) * mm, "radius": 5.05 * mm});
            skCircle(sketch, "E72.2.0", {"center": v(-104.43, 43.25) * mm, "radius": 5.05 * mm});
            skCircle(sketch, "E72.3.0", {"center": v(-104.43, -43.25) * mm, "radius": 5.05 * mm});
            skCircle(sketch, "E72.4.0", {"center": v(-43.25, -104.43) * mm, "radius": 5.05 * mm});
            skCircle(sketch, "E72.5.0", {"center": v(43.25, -104.43) * mm, "radius": 5.05 * mm});
            skCircle(sketch, "E72.6.0", {"center": v(104.43, -43.25) * mm, "radius": 5.05 * mm});
            skCircle(sketch, "E72.7.0", {"center": v(104.43, 43.25) * mm, "radius": 5.05 * mm});
            skPoint(sketch, "E72.center", {"position": v(0, 0) * mm});
            skSolve(sketch);
        }
        {
            var Q0;
            Q0=qSketchRegion(id+"F19",true);
            extrude(context, id + "F20", {"entities" : qUnion([Q0]), "operationType" : NewBodyOperationType.REMOVE, "oppositeDirection" : true, "depth" : 15.88 * mm});
        }
        {
            var Q0;
            Q0=qCreatedBy(makeId("Front.planeOp"),FACE);
            var sketch = newSketch(context, id + "F21", { "sketchPlane" : qUnion([Q0])});
            skCircle(sketch, "E73", {"center": v(-43.25, 104.43) * mm, "radius": 5.59 * mm});
            skCircle(sketch, "E74.1.0", {"center": v(-104.43, 43.25) * mm, "radius": 5.59 * mm});
            skCircle(sketch, "E74.2.0", {"center": v(-104.43, -43.25) * mm, "radius": 5.59 * mm});
            skCircle(sketch, "E74.3.0", {"center": v(-43.25, -104.43) * mm, "radius": 5.59 * mm});
            skCircle(sketch, "E74.4.0", {"center": v(43.25, -104.43) * mm, "radius": 5.59 * mm});
            skCircle(sketch, "E74.5.0", {"center": v(104.43, -43.25) * mm, "radius": 5.59 * mm});
            skCircle(sketch, "E74.6.0", {"center": v(104.43, 43.25) * mm, "radius": 5.59 * mm});
            skCircle(sketch, "E74.7.0", {"center": v(43.25, 104.43) * mm, "radius": 5.59 * mm});
            skPoint(sketch, "E74.center", {"position": v(0, 0) * mm});
            skSolve(sketch);
        }
        {
            var Q0;
            Q0=qSketchRegion(id+"F21",true);
            extrude(context, id + "F22", {"entities" : qUnion([Q0]), "operationType" : NewBodyOperationType.REMOVE, "oppositeDirection" : true, "depth" : 1.7 * mm});
        }
    });
